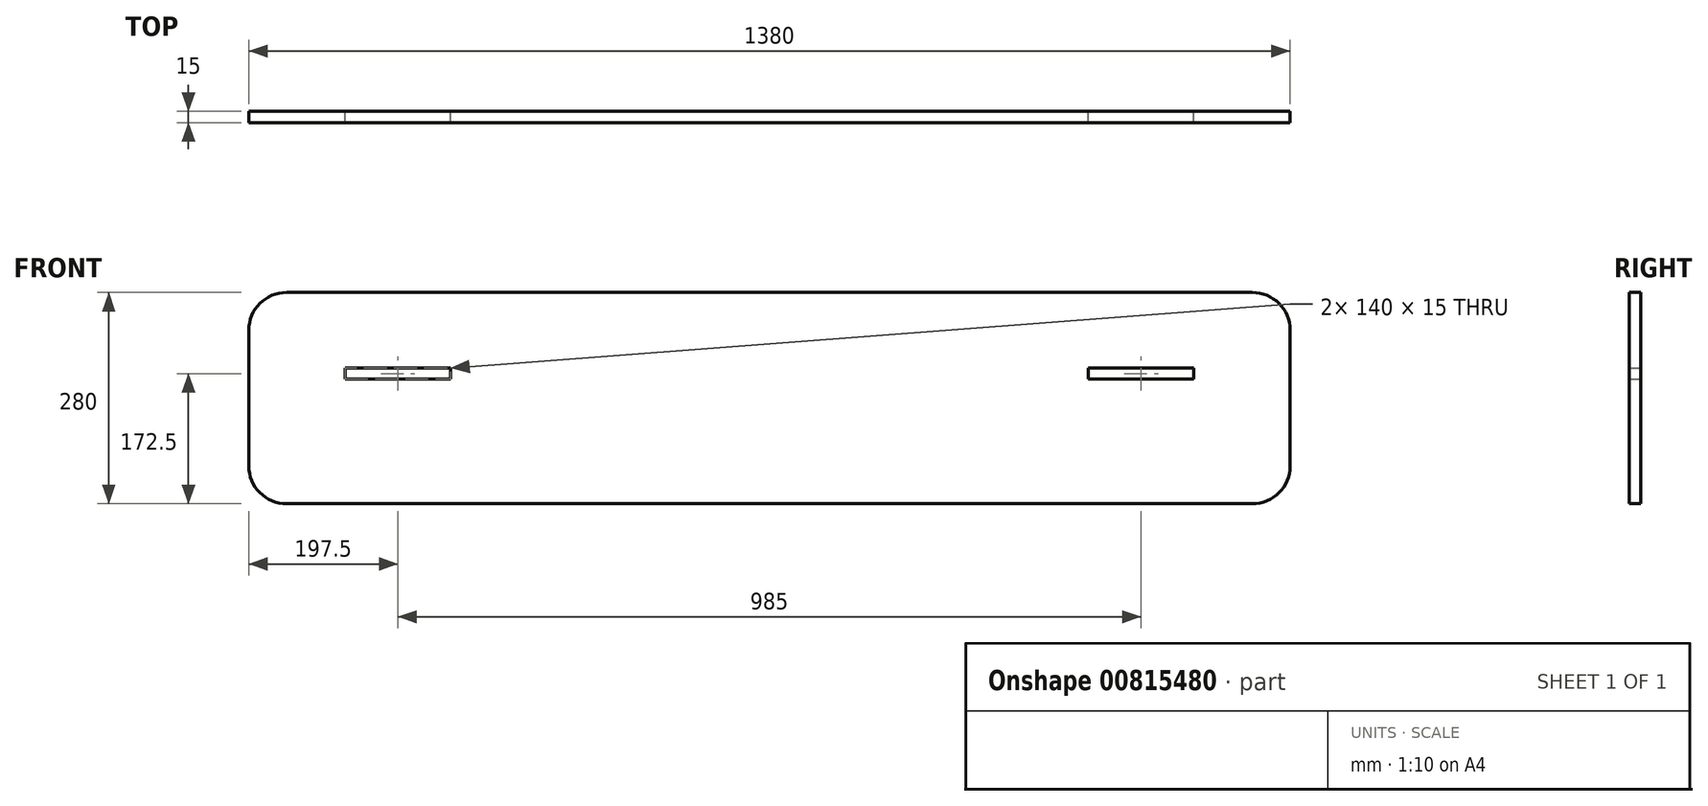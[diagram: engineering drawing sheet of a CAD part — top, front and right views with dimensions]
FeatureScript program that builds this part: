
annotation { "Feature Type Name" : "Feature", "Feature Type Description" : "" }
export const myFeature = defineFeature(function(context is Context, id is Id, definition is map)
    precondition{}
    {
        {
            var Q0;
            Q0=qCreatedBy(makeId("Front.planeOp"),FACE);
            var sketch = newSketch(context, id + "F0", { "sketchPlane" : qUnion([Q0])});
            skLineSegment(sketch, "E0.bottom", {"start": v(-640, 140) * mm, "end": v(640, 140) * mm});
            skLineSegment(sketch, "E0.top", {"start": v(-640, -140) * mm, "end": v(640, -140) * mm});
            skLineSegment(sketch, "E0.left", {"start": v(-690, 90) * mm, "end": v(-690, -90) * mm});
            skLineSegment(sketch, "E0.right", {"start": v(690, 90) * mm, "end": v(690, -90) * mm});
            skPoint(sketch, "E0.middle", {"position": v(0, 0) * mm});
            skLineSegment(sketch, "E1.bottom", {"start": v(-562.5, 40) * mm, "end": v(-422.5, 40) * mm});
            skLineSegment(sketch, "E1.top", {"start": v(-562.5, 25) * mm, "end": v(-422.5, 25) * mm});
            skLineSegment(sketch, "E1.left", {"start": v(-562.5, 40) * mm, "end": v(-562.5, 25) * mm});
            skLineSegment(sketch, "E1.right", {"start": v(-422.5, 40) * mm, "end": v(-422.5, 25) * mm});
            skLineSegment(sketch, "E2", {"start": v(562.5, 40) * mm, "end": v(422.5, 40) * mm});
            skLineSegment(sketch, "E3", {"start": v(422.5, 40) * mm, "end": v(422.5, 25) * mm});
            skLineSegment(sketch, "E4", {"start": v(422.5, 25) * mm, "end": v(562.5, 25) * mm});
            skLineSegment(sketch, "E5", {"start": v(562.5, 25) * mm, "end": v(562.5, 40) * mm});
            skPoint(sketch, "E6.visualSharp", {"position": v(-690, 140) * mm});
            skArc(sketch, "E6.filletArc", {"start": v(-640, 140) * mm, "mid": v(-675.36, 125.36) * mm, "end": v(-690, 90) * mm});
            skPoint(sketch, "E7.visualSharp", {"position": v(-690, -140) * mm});
            skArc(sketch, "E7.filletArc", {"start": v(-690, -90) * mm, "mid": v(-675.36, -125.36) * mm, "end": v(-640, -140) * mm});
            skPoint(sketch, "E8.visualSharp", {"position": v(690, 140) * mm});
            skArc(sketch, "E8.filletArc", {"start": v(690, 90) * mm, "mid": v(675.36, 125.36) * mm, "end": v(640, 140) * mm});
            skPoint(sketch, "E9.visualSharp", {"position": v(690, -140) * mm});
            skArc(sketch, "E9.filletArc", {"start": v(640, -140) * mm, "mid": v(675.36, -125.36) * mm, "end": v(690, -90) * mm});
            skSolve(sketch);
        }
        {
            var Q0;
            Q0=makeQuery(id+"F0.imprint","IMPRINT",FACE,{"disambiguationData":[TD([[makeQuery(id+"F0.imprint","IMPRINT",EDGE,{"derivedFrom":sQuery(id+"F0.wireOp",EDGE,"E0.bottom")}),-1.0]])]});
            extrude(context, id + "F1", {"entities" : qUnion([Q0]), "depth" : 15 * mm, "offsetDistance" : 25 * mm});
        }
    });
